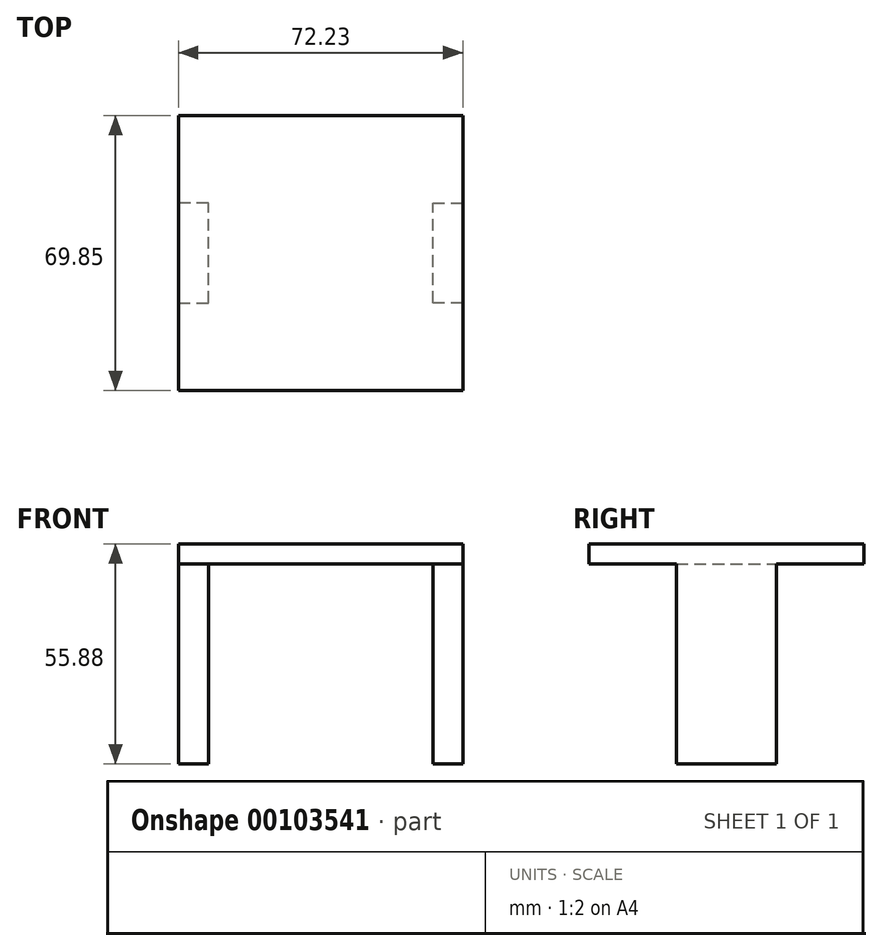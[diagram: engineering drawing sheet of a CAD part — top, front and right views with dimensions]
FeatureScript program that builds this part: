
annotation { "Feature Type Name" : "Feature", "Feature Type Description" : "" }
export const myFeature = defineFeature(function(context is Context, id is Id, definition is map)
    precondition{}
    {
        {
            var Q0;
            Q0=qCreatedBy(makeId("Top.planeOp"),FACE);
            var sketch = newSketch(context, id + "F0", { "sketchPlane" : qUnion([Q0])});
            skLineSegment(sketch, "E0.bottom", {"start": v(-95.09, -34.56) * mm, "end": v(-22.86, -34.56) * mm});
            skLineSegment(sketch, "E0.top", {"start": v(-95.09, 35.29) * mm, "end": v(-22.86, 35.29) * mm});
            skLineSegment(sketch, "E0.left", {"start": v(-95.09, -34.56) * mm, "end": v(-95.09, 35.29) * mm});
            skLineSegment(sketch, "E0.right", {"start": v(-22.86, -34.56) * mm, "end": v(-22.86, 35.29) * mm});
            skSolve(sketch);
        }
        {
            var Q0;
            Q0=makeQuery(id+"F0.imprint","IMPRINT",FACE,{"disambiguationData":[TD([[makeQuery(id+"F0.imprint","IMPRINT",EDGE,{"derivedFrom":sQuery(id+"F0.wireOp",EDGE,"E0.bottom")}),1.0]])]});
            extrude(context, id + "F1", {"entities" : qUnion([Q0]), "depth" : 5.08 * mm});
        }
        {
            var Q0;
            Q0=makeQuery(id+"F1.opExtrude","CAP_FACE",FACE,{"disambiguationData":[OSD([sQuery(id+"F0.wireOp",EDGE,"E0.bottom"),sQuery(id+"F0.wireOp",EDGE,"E0.top"),sQuery(id+"F0.wireOp",EDGE,"E0.left"),sQuery(id+"F0.wireOp",EDGE,"E0.right")])],"isStart":true});
            var sketch = newSketch(context, id + "F2", { "sketchPlane" : qUnion([Q0])});
            skPoint(sketch, "E1", {"position": v(-95.09, -0.36) * mm});
            skPoint(sketch, "E2", {"position": v(-22.86, -0.36) * mm});
            skLineSegment(sketch, "E3", {"start": v(-95.09, -0.36) * mm, "end": v(-95.09, 12.34) * mm});
            skLineSegment(sketch, "E4", {"start": v(-95.09, 12.34) * mm, "end": v(-95.09, -13.06) * mm});
            skLineSegment(sketch, "E5", {"start": v(-22.86, -0.36) * mm, "end": v(-22.86, 12.34) * mm});
            skLineSegment(sketch, "E6", {"start": v(-22.86, 12.34) * mm, "end": v(-22.86, -13.06) * mm});
            skLineSegment(sketch, "E7", {"start": v(-95.09, 12.34) * mm, "end": v(-87.47, 12.34) * mm});
            skLineSegment(sketch, "E8", {"start": v(-87.47, 12.34) * mm, "end": v(-87.47, -13.06) * mm});
            skLineSegment(sketch, "E9", {"start": v(-87.47, -13.06) * mm, "end": v(-95.09, -13.06) * mm});
            skLineSegment(sketch, "E10", {"start": v(-22.86, 12.34) * mm, "end": v(-30.48, 12.34) * mm});
            skLineSegment(sketch, "E11", {"start": v(-30.48, 12.34) * mm, "end": v(-30.48, -13.06) * mm});
            skLineSegment(sketch, "E12", {"start": v(-30.48, -13.06) * mm, "end": v(-22.86, -13.06) * mm});
            skSolve(sketch);
        }
        {
            var Q0;
            {var subQ0=sQuery(id+"F2.wireOp",EDGE,"E7");Q0=makeQuery(id+"F2.imprint","IMPRINT",FACE,{"disambiguationData":[TD([[makeQuery(id+"F2.imprint","IMPRINT",EDGE,{"derivedFrom":subQ0}),-1.0]])]});}
            var Q1;
            {var subQ0=sQuery(id+"F2.wireOp",EDGE,"E10");Q1=makeQuery(id+"F2.imprint","IMPRINT",FACE,{"disambiguationData":[TD([[makeQuery(id+"F2.imprint","IMPRINT",EDGE,{"derivedFrom":subQ0}),1.0]])]});}
            extrude(context, id + "F3", {"entities" : qUnion([Q0, Q1]), "operationType" : NewBodyOperationType.ADD, "depth" : 50.8 * mm});
        }
    });
